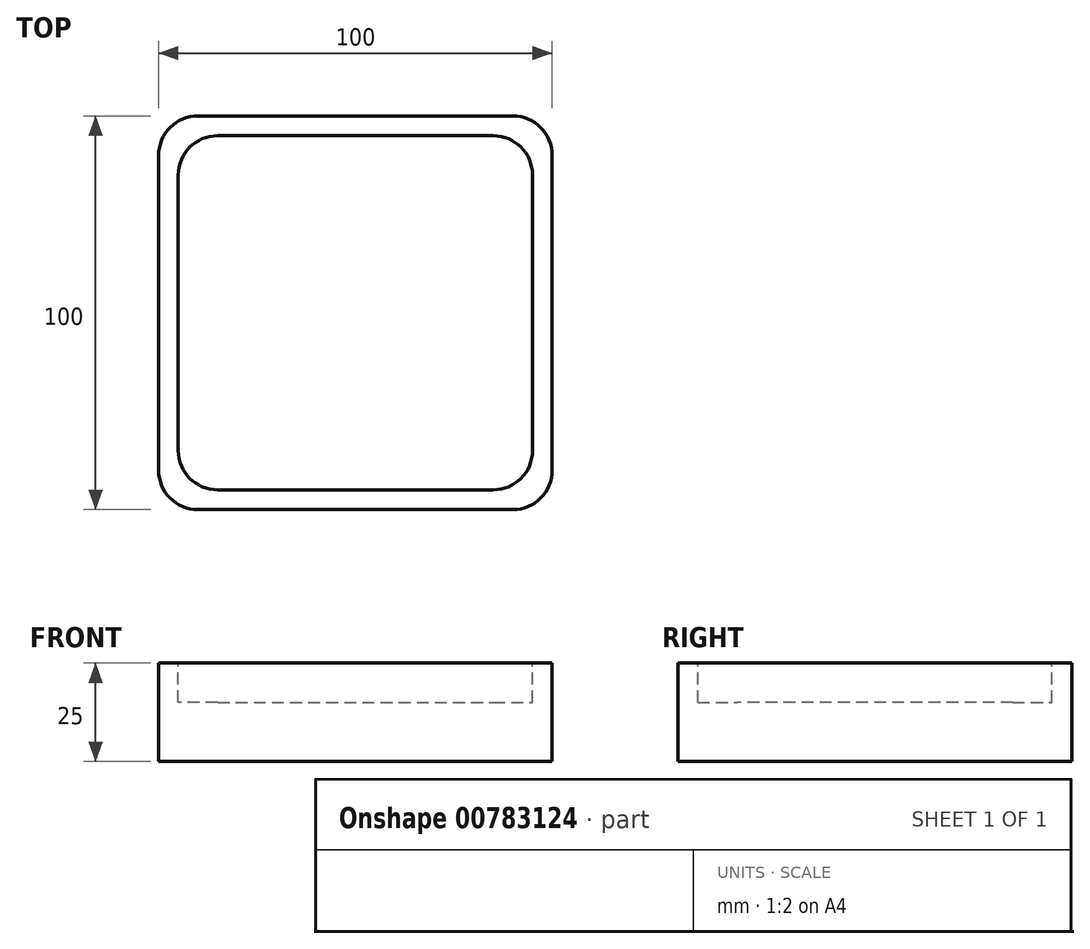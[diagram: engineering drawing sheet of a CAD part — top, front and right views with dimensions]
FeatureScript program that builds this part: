
annotation { "Feature Type Name" : "Feature", "Feature Type Description" : "" }
export const myFeature = defineFeature(function(context is Context, id is Id, definition is map)
    precondition{}
    {
        {
            var Q0;
            Q0=qCreatedBy(makeId("Top.planeOp"),FACE);
            var sketch = newSketch(context, id + "F0", { "sketchPlane" : qUnion([Q0])});
            skLineSegment(sketch, "E0.bottom", {"start": v(-50, 50) * mm, "end": v(50, 50) * mm});
            skLineSegment(sketch, "E0.top", {"start": v(-50, -50) * mm, "end": v(50, -50) * mm});
            skLineSegment(sketch, "E0.left", {"start": v(-50, 50) * mm, "end": v(-50, -50) * mm});
            skLineSegment(sketch, "E0.right", {"start": v(50, 50) * mm, "end": v(50, -50) * mm});
            skPoint(sketch, "E0.middle", {"position": v(0, 0) * mm});
            skSolve(sketch);
        }
        {
            var Q0;
            Q0 = qSketchRegion(id + "F0", true);
            extrude(context, id + "F1", {"entities" : qUnion([Q0]), "depth" : 25 * mm, "offsetDistance" : 25 * mm});
        }
        {
            var Q0;
            Q0=makeQuery(id+"F1.opExtrude","CAP_FACE",FACE,{"disambiguationData":[OSD([sQuery(id+"F0.wireOp",EDGE,"E0.bottom"),sQuery(id+"F0.wireOp",EDGE,"E0.top"),sQuery(id+"F0.wireOp",EDGE,"E0.left"),sQuery(id+"F0.wireOp",EDGE,"E0.right")])],"isStart":false});
            var sketch = newSketch(context, id + "F2", { "sketchPlane" : qUnion([Q0])});
            skLineSegment(sketch, "E1.bottom", {"start": v(-45, 45) * mm, "end": v(45, 45) * mm});
            skLineSegment(sketch, "E1.top", {"start": v(-45, -45) * mm, "end": v(45, -45) * mm});
            skLineSegment(sketch, "E1.left", {"start": v(-45, 45) * mm, "end": v(-45, -45) * mm});
            skLineSegment(sketch, "E1.right", {"start": v(45, 45) * mm, "end": v(45, -45) * mm});
            skPoint(sketch, "E1.middle", {"position": v(0, 0) * mm});
            skSolve(sketch);
        }
        {
            var Q0;
            Q0 = qSketchRegion(id + "F2", true);
            extrude(context, id + "F3", {"entities" : qUnion([Q0]), "operationType" : NewBodyOperationType.REMOVE, "oppositeDirection" : true, "depth" : 10 * mm, "offsetDistance" : 25 * mm});
        }
        {
            var Q0;
            Q0=makeQuery(id+"F1.opExtrude","SWEPT_EDGE",EDGE,{"disambiguationData":[OSD([sQuery(id+"F0.wireOp",EDGE,"E0.bottom"),sQuery(id+"F0.wireOp",EDGE,"E0.right")])]});
            var Q1;
            Q1=makeQuery(id+"F3.boolean.opBoolean","COPY",EDGE,{"derivedFrom":makeQuery(id+"F3.opExtrude","SWEPT_EDGE",EDGE,{"disambiguationData":[OSD([sQuery(id+"F2.wireOp",EDGE,"E1.bottom"),sQuery(id+"F2.wireOp",EDGE,"E1.right")])]})});
            var Q2;
            Q2=makeQuery(id+"F3.boolean.opBoolean","COPY",EDGE,{"derivedFrom":makeQuery(id+"F3.opExtrude","SWEPT_EDGE",EDGE,{"disambiguationData":[OSD([sQuery(id+"F2.wireOp",EDGE,"E1.bottom"),sQuery(id+"F2.wireOp",EDGE,"E1.left")])]})});
            var Q3;
            Q3=makeQuery(id+"F1.opExtrude","SWEPT_EDGE",EDGE,{"disambiguationData":[OSD([sQuery(id+"F0.wireOp",EDGE,"E0.bottom"),sQuery(id+"F0.wireOp",EDGE,"E0.left")])]});
            var Q4;
            Q4=makeQuery(id+"F1.opExtrude","SWEPT_EDGE",EDGE,{"disambiguationData":[OSD([sQuery(id+"F0.wireOp",EDGE,"E0.top"),sQuery(id+"F0.wireOp",EDGE,"E0.left")])]});
            var Q5;
            Q5=makeQuery(id+"F3.boolean.opBoolean","COPY",EDGE,{"derivedFrom":makeQuery(id+"F3.opExtrude","SWEPT_EDGE",EDGE,{"disambiguationData":[OSD([sQuery(id+"F2.wireOp",EDGE,"E1.top"),sQuery(id+"F2.wireOp",EDGE,"E1.left")])]})});
            var Q6;
            Q6=makeQuery(id+"F1.opExtrude","SWEPT_EDGE",EDGE,{"disambiguationData":[OSD([sQuery(id+"F0.wireOp",EDGE,"E0.top"),sQuery(id+"F0.wireOp",EDGE,"E0.right")])]});
            var Q7;
            Q7=makeQuery(id+"F3.boolean.opBoolean","COPY",EDGE,{"derivedFrom":makeQuery(id+"F3.opExtrude","SWEPT_EDGE",EDGE,{"disambiguationData":[OSD([sQuery(id+"F2.wireOp",EDGE,"E1.top"),sQuery(id+"F2.wireOp",EDGE,"E1.right")])]})});
            fillet(context, id + "F4", {"entities" : qUnion([Q0, Q1, Q2, Q3, Q4, Q5, Q6, Q7]), "radius" : 10 * mm, "tangentPropagation" : true, "allowEdgeOverflow" : false});
        }
    });
